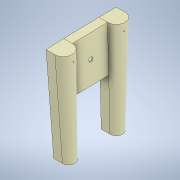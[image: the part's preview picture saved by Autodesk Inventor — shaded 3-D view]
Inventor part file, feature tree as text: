
AUTODESK INVENTOR PART (.ipt)
format: ipt  version: 2020.3 (Build 243373000, 373)  size: 200,704 bytes
history: native  units: mm
features: sketch x5, other x4, plane x3, extrude x3, shell x2, reference x2, loft x1, mirror x1, projected_geometry x1
ambient origin geometry x8: Origin, YZ Plane, XZ Plane, XY Plane, X Axis, Y Axis, Z Axis, Center Point
bodies: Solid1 (feature_tree)
feature tree (22):
  sketch  "Sketch1"  dims[d0=50.0mm d1=50.0mm d2=25.0mm]
  plane  "Work Plane2"
  loft  "Loft1"
  shell  "Shell1"  Thickness=25.0mm
  plane  "Work Plane4"
  mirror  "Mirror1"
  extrude  "Extrusion1"  Depth=35.714286mm
  shell  "Shell2"  Thickness=0.0mm
  extrude  "Extrusion2"  Depth=2.0mm
  extrude  "Extrusion3"  Depth=132.0mm
  plane  "Work Plane1"
  sketch  "Sketch2"  dims[d3=280.0mm d4=35.714286mm d5=0.0mm d6=90.0deg]
  sketch  "Sketch3"  dims[d7=0.0mm d8=90.0deg d9=2.0mm]
  projected_geometry  "Projected Loop1"
  sketch  "Sketch4"  dims[d11=50.0mm d12=132.0mm]
  sketch  "Sketch5"  dims[d13=10.0mm d14=0.0mm d15=2.0mm d16=12.0mm d17=25.0mm d18=0.0mm d19=0.0mm d20=0.0mm]
  reference  "Reference1"
  reference  "Reference2"
  other  "<userpath>\Documents\Inventor\TheArch\R&D\Alpha0\Structura\TestSpatiu.iam"
  other  "TestSpatiu.iam"
  other  "PrindereDisc:1"
  other  "PrindereDisc:2"
